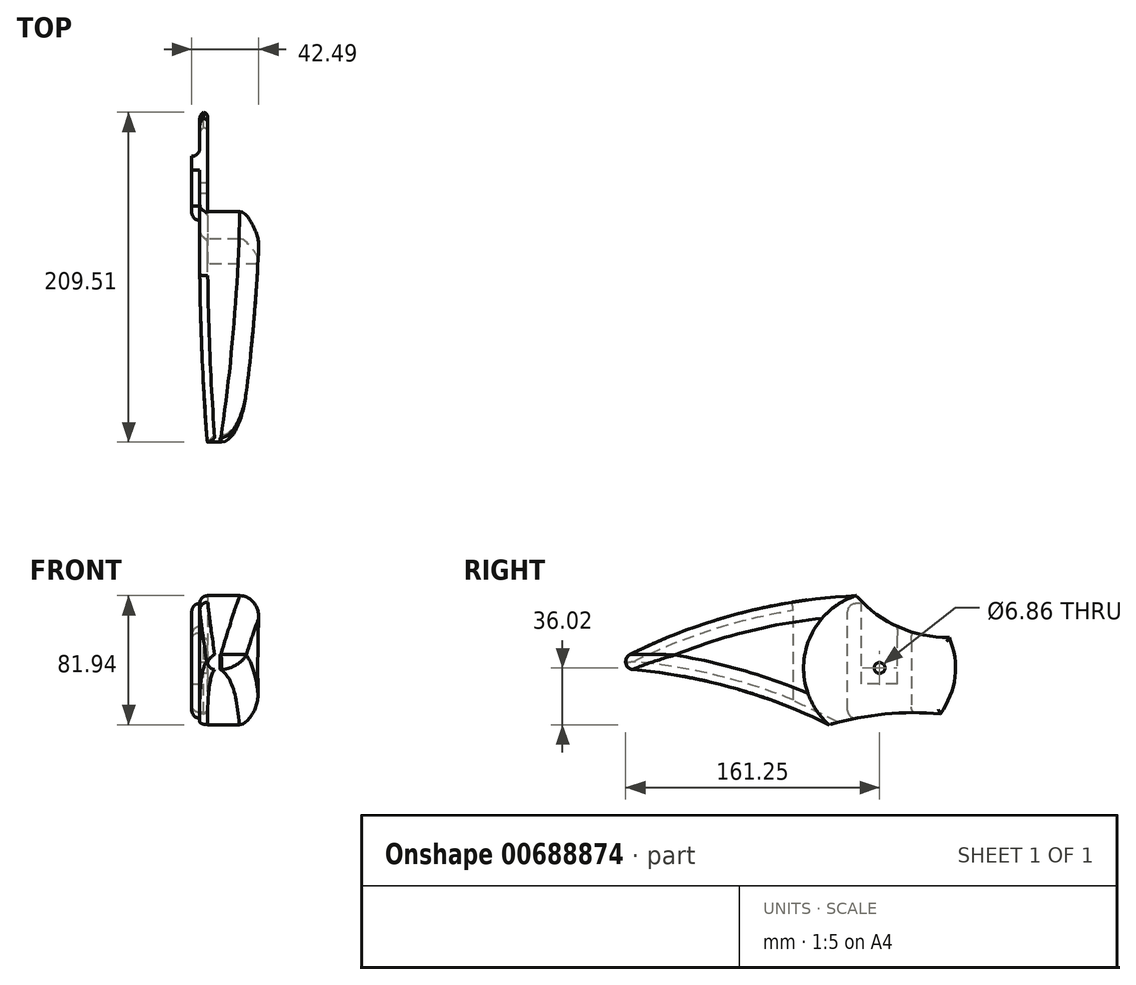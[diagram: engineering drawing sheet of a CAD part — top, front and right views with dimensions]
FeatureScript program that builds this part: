
annotation { "Feature Type Name" : "Feature", "Feature Type Description" : "" }
export const myFeature = defineFeature(function(context is Context, id is Id, definition is map)
    precondition{}
    {
        {
            var Q0;
            Q0=qCreatedBy(makeId("Right.planeOp"),FACE);
            var sketch = newSketch(context, id + "F0", { "sketchPlane" : qUnion([Q0])});
            skArc(sketch, "E0.0", {"start": v(-14.83, 45.92) * mm, "mid": v(-47.22, 9.96) * mm, "end": v(-32.12, -36.02) * mm});
            skArc(sketch, "E1", {"start": v(-14.83, 45.92) * mm, "mid": v(-97.33, 32.4) * mm, "end": v(-174.4, 0) * mm});
            skArc(sketch, "E2", {"start": v(-32.12, -36.02) * mm, "mid": v(-101.34, -10.43) * mm, "end": v(-174.4, 0) * mm});
            skArc(sketch, "E3", {"start": v(38.54, -29.05) * mm, "mid": v(2.9, -29.35) * mm, "end": v(-32.12, -36.02) * mm});
            skArc(sketch, "E4", {"start": v(-14.83, 45.92) * mm, "mid": v(11.77, 26.14) * mm, "end": v(44.22, 19.34) * mm});
            skArc(sketch, "E5.trimOffspring", {"start": v(38.54, -29.05) * mm, "mid": v(47.93, -5.62) * mm, "end": v(44.22, 19.34) * mm});
            skCircle(sketch, "E6", {"center": v(0, 0) * mm, "radius": 3.43 * mm});
            skSolve(sketch);
        }
        {
            var Q0;
            Q0=makeQuery(id+"F0.imprint","IMPRINT",FACE,{"disambiguationData":[TD([[makeQuery(id+"F0.imprint","IMPRINT",EDGE,{"derivedFrom":sQuery(id+"F0.wireOp",EDGE,"E0.0")}),1.0]])]});
            extrude(context, id + "F1", {"entities" : qUnion([Q0]), "depth" : 4.83 * mm, "offsetDistance" : 25.4 * mm});
        }
        {
            var Q0;
            Q0=makeQuery(id+"F0.imprint","IMPRINT",FACE,{"disambiguationData":[TD([[makeQuery(id+"F0.imprint","IMPRINT",EDGE,{"derivedFrom":sQuery(id+"F0.wireOp",EDGE,"E0.0")}),-1.0]])]});
            extrude(context, id + "F2", {"entities" : qUnion([Q0]), "operationType" : NewBodyOperationType.ADD, "depth" : 38.1 * mm, "offsetDistance" : 25.4 * mm});
        }
        {
            var Q0;
            Q0=makeQuery(id+"F1.opExtrude","CAP_EDGE",EDGE,{"disambiguationData":[OSD([sQuery(id+"F0.wireOp",EDGE,"E4")])],"isStart":false});
            var Q1;
            Q1=makeQuery(id+"F1.opExtrude","CAP_EDGE",EDGE,{"disambiguationData":[OSD([sQuery(id+"F0.wireOp",EDGE,"E3")])],"isStart":false});
            var Q2;
            Q2=makeQuery(id+"F1.opExtrude","CAP_EDGE",EDGE,{"disambiguationData":[OSD([sQuery(id+"F0.wireOp",EDGE,"E5.trimOffspring")])],"isStart":false});
            fillet(context, id + "F3", {"entities" : qUnion([Q0, Q1, Q2]), "radius" : 2.54 * mm, "tangentPropagation" : true, "allowEdgeOverflow" : false});
        }
        {
            var Q0;
            Q0=makeQuery(id+"F2.boolean.opBoolean","SPLIT",EDGE,{"derivedFrom":makeQuery(id+"F2.opExtrude","SWEPT_EDGE",EDGE,{"disambiguationData":[OSD([sQuery(id+"F0.wireOp",EDGE,"E0.0"),sQuery(id+"F0.wireOp",EDGE,"E1"),sQuery(id+"F0.wireOp",EDGE,"E4")])]})});
            cPlane(context, id + "F4", {"entities" : qUnion([Q0]), "cplaneType" : CPlaneType.LINE_ANGLE, "offset" : 0 * mm, "angle" : 90 * degree, "width" : 152.4 * mm, "height" : 152.4 * mm});
        }
        {
            var Q0;
            Q0=qCreatedBy(id+"F4.planeOp",FACE);
            var sketch = newSketch(context, id + "F5", { "sketchPlane" : qUnion([Q0])});
            skLineSegment(sketch, "E7", {"start": v(22.21, -178.04) * mm, "end": v(43.85, -178.04) * mm});
            skLineSegment(sketch, "E8", {"start": v(43.85, -178.04) * mm, "end": v(43.85, -14.83) * mm});
            skLineSegment(sketch, "E9", {"start": v(43.85, -14.83) * mm, "end": v(38.1, -14.83) * mm});
            skArc(sketch, "E10", {"start": v(22.21, -178.04) * mm, "mid": v(33.2, -96.73) * mm, "end": v(38.1, -14.83) * mm});
            skArc(sketch, "E11", {"start": v(0, -14.83) * mm, "mid": v(0.95, -94.12) * mm, "end": v(5.71, -173.26) * mm});
            skLineSegment(sketch, "E12", {"start": v(0, -14.83) * mm, "end": v(-6.93, -14.83) * mm});
            skLineSegment(sketch, "E13", {"start": v(-6.93, -14.83) * mm, "end": v(-6.93, -179.8) * mm});
            skLineSegment(sketch, "E14", {"start": v(-6.93, -179.8) * mm, "end": v(5.71, -179.8) * mm});
            skLineSegment(sketch, "E15", {"start": v(5.71, -179.8) * mm, "end": v(5.71, -173.26) * mm});
            skSolve(sketch);
        }
        {
            var Q0;
            Q0=qSketchRegion(id+"F5",true);
            extrude(context, id + "F6", {"entities" : qUnion([Q0]), "operationType" : NewBodyOperationType.REMOVE, "endBound" : BoundingType.THROUGH_ALL, "oppositeDirection" : true, "depth" : 25.4 * mm, "offsetDistance" : 25.4 * mm});
        }
        {
            var Q0;
            Q0=makeQuery(id+"F6.boolean.opBoolean","INTERSECT",EDGE,{"derivedFrom":[makeQuery(id+"F2.opExtrude","SWEPT_FACE",FACE,{"disambiguationData":[OSD([sQuery(id+"F0.wireOp",EDGE,"E1")])]}),makeQuery(id+"F6.opExtrude","SWEPT_FACE",FACE,{"disambiguationData":[OSD([sQuery(id+"F5.wireOp",EDGE,"E10")])]})]});
            var Q1;
            Q1=makeQuery(id+"F6.boolean.opBoolean","INTERSECT",EDGE,{"derivedFrom":[makeQuery(id+"F2.opExtrude","SWEPT_FACE",FACE,{"disambiguationData":[OSD([sQuery(id+"F0.wireOp",EDGE,"E2")])]}),makeQuery(id+"F6.opExtrude","SWEPT_FACE",FACE,{"disambiguationData":[OSD([sQuery(id+"F5.wireOp",EDGE,"E10")])]})]});
            fillet(context, id + "F7", {"entities" : qUnion([Q0, Q1]), "radius" : 12.7 * mm, "tangentPropagation" : true, "allowEdgeOverflow" : false});
        }
        {
            var Q0;
            Q0=makeQuery(id+"F2.opExtrude","SWEPT_EDGE",EDGE,{"disambiguationData":[OSD([sQuery(id+"F0.wireOp",EDGE,"E1"),sQuery(id+"F0.wireOp",EDGE,"E2")])]});
            var Q1;
            Q1=makeQuery(id+"F6.boolean.opBoolean","INTERSECT",EDGE,{"derivedFrom":[makeQuery(id+"F2.opExtrude","SWEPT_FACE",FACE,{"disambiguationData":[OSD([sQuery(id+"F0.wireOp",EDGE,"E1")])]}),makeQuery(id+"F6.opExtrude","SWEPT_FACE",FACE,{"disambiguationData":[OSD([sQuery(id+"F5.wireOp",EDGE,"E11")])]})]});
            var Q2;
            Q2=makeQuery(id+"F6.boolean.opBoolean","INTERSECT",EDGE,{"derivedFrom":[makeQuery(id+"F2.opExtrude","SWEPT_FACE",FACE,{"disambiguationData":[OSD([sQuery(id+"F0.wireOp",EDGE,"E2")])]}),makeQuery(id+"F6.opExtrude","SWEPT_FACE",FACE,{"disambiguationData":[OSD([sQuery(id+"F5.wireOp",EDGE,"E11")])]})]});
            fillet(context, id + "F8", {"entities" : qUnion([Q0, Q1, Q2]), "radius" : 5.08 * mm, "tangentPropagation" : true, "allowEdgeOverflow" : false});
        }
        {
            var Q0;
            Q0=makeQuery(id+"F0.imprint","IMPRINT",FACE,{"disambiguationData":[TD([[makeQuery(id+"F0.imprint","IMPRINT",EDGE,{"derivedFrom":sQuery(id+"F0.wireOp",EDGE,"E0.0")}),1.0]])]});
            var sketch = newSketch(context, id + "F9", { "sketchPlane" : qUnion([Q0])});
            skCircle(sketch, "E16.0", {"center": v(0, 0) * mm, "radius": 3.43 * mm});
            skArc(sketch, "E17.0", {"start": v(-14.83, 45.92) * mm, "mid": v(11.77, 26.14) * mm, "end": v(44.22, 19.34) * mm});
            skArc(sketch, "E18.0", {"start": v(38.54, -29.05) * mm, "mid": v(2.9, -29.35) * mm, "end": v(-32.12, -36.02) * mm});
            skLineSegment(sketch, "E19", {"start": v(20.32, 22.88) * mm, "end": v(20.32, -28.4) * mm});
            skArc(sketch, "E20.0", {"start": v(-54.78, 36.72) * mm, "mid": v(-32.55, 39.58) * mm, "end": v(-10.18, 41.02) * mm});
            skLineSegment(sketch, "E21", {"start": v(-20.32, -33.04) * mm, "end": v(-20.32, 40.55) * mm});
            skLineSegment(sketch, "E22.bottom", {"start": v(11.43, -10.16) * mm, "end": v(-11.43, -10.16) * mm});
            skLineSegment(sketch, "E22.top", {"start": v(11.43, 42.44) * mm, "end": v(-11.43, 42.44) * mm});
            skLineSegment(sketch, "E22.left", {"start": v(11.43, -10.16) * mm, "end": v(11.43, 42.44) * mm});
            skLineSegment(sketch, "E22.right", {"start": v(-11.43, -10.16) * mm, "end": v(-11.43, 42.44) * mm});
            skSolve(sketch);
        }
        {
            var Q0;
            {var subQ4=sQuery(id+"F9.wireOp",EDGE,"E19");Q0=makeQuery(id+"F9.imprint","IMPRINT",FACE,{"disambiguationData":[TD([[makeQuery(id+"F9.imprint","IMPRINT",EDGE,{"derivedFrom":subQ4}),-1.0]])]});}
            extrude(context, id + "F10", {"entities" : qUnion([Q0]), "operationType" : NewBodyOperationType.ADD, "oppositeDirection" : true, "depth" : 5.08 * mm, "offsetDistance" : 25.4 * mm});
        }
        {
            var Q0;
            Q0=makeQuery(id+"F10.opExtrude","CAP_EDGE",EDGE,{"disambiguationData":[OSD([sQuery(id+"F9.wireOp",EDGE,"E19")])],"isStart":true});
            var Q1;
            Q1=makeQuery(id+"F10.opExtrude","CAP_EDGE",EDGE,{"disambiguationData":[OSD([sQuery(id+"F9.wireOp",EDGE,"E21")])],"isStart":false});
            fillet(context, id + "F11", {"entities" : qUnion([Q0, Q1]), "radius" : 5.08 * mm, "tangentPropagation" : true, "allowEdgeOverflow" : false});
        }
        {
            var Q0;
            Q0=makeQuery(id+"F1.opExtrude","CAP_EDGE",EDGE,{"disambiguationData":[OSD([sQuery(id+"F0.wireOp",EDGE,"E5.trimOffspring")])],"isStart":true});
            var Q1;
            Q1=makeQuery(id+"F10.opExtrude","CAP_EDGE",EDGE,{"disambiguationData":[OSD([sQuery(id+"F9.wireOp",EDGE,"E18.0")])],"isStart":false});
            var Q2;
            Q2=makeQuery(id+"F10.opExtrude","CAP_EDGE",EDGE,{"disambiguationData":[OSD([sQuery(id+"F9.wireOp",EDGE,"E17.0")])],"isStart":false});
            var Q3;
            Q3=makeQuery(id+"F10.opExtrude","CAP_EDGE",EDGE,{"disambiguationData":[OSD([sQuery(id+"F9.wireOp",EDGE,"E20.0")])],"isStart":false});
            fillet(context, id + "F12", {"entities" : qUnion([Q0, Q1, Q2, Q3]), "radius" : 5.08 * mm, "tangentPropagation" : true, "allowEdgeOverflow" : false});
        }
    });
